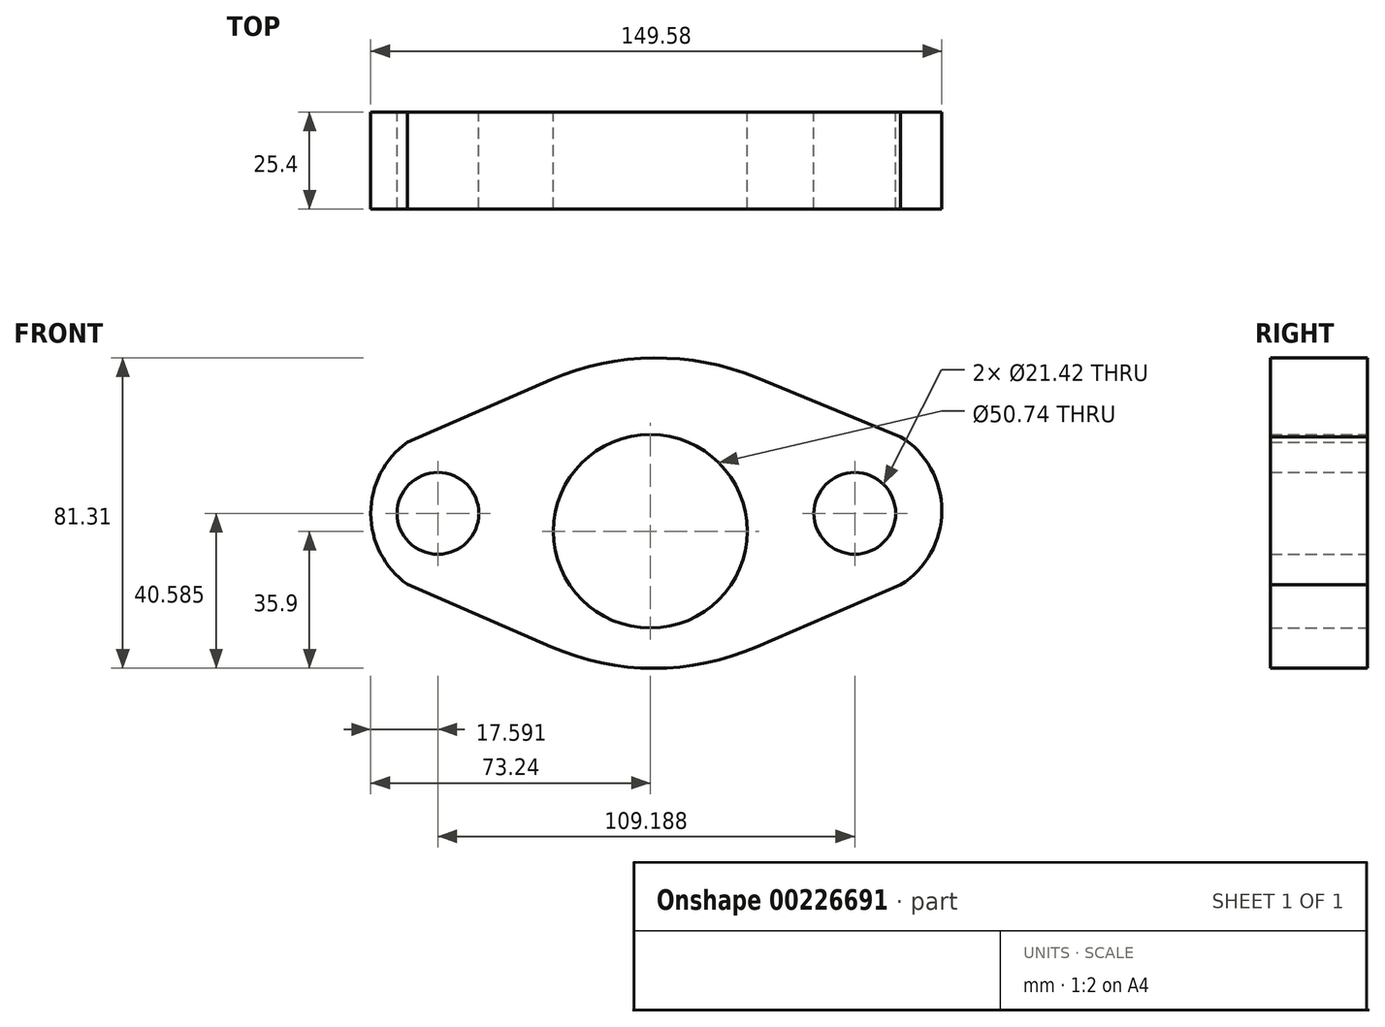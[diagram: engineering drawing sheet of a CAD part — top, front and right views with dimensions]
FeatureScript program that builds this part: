
annotation { "Feature Type Name" : "Feature", "Feature Type Description" : "" }
export const myFeature = defineFeature(function(context is Context, id is Id, definition is map)
    precondition{}
    {
        {
            var Q0;
            Q0=qCreatedBy(makeId("Front.planeOp"),FACE);
            var sketch = newSketch(context, id + "F0", { "sketchPlane" : qUnion([Q0])});
            skCircle(sketch, "E0", {"center": v(0, 0) * mm, "radius": 25.37 * mm});
            skArc(sketch, "E1", {"start": v(27.87, 40.23) * mm, "mid": v(0.85, 45.4) * mm, "end": v(-26.06, 39.65) * mm});
            skLineSegment(sketch, "E2", {"start": v(-26.06, 39.65) * mm, "end": v(-63.66, 23.27) * mm});
            skArc(sketch, "E3", {"start": v(-63.66, 23.27) * mm, "mid": v(-73.24, 4.68) * mm, "end": v(-63.66, -13.9) * mm});
            skLineSegment(sketch, "E4", {"start": v(27.87, 40.23) * mm, "end": v(65.52, 24.79) * mm});
            skLineSegment(sketch, "E5", {"start": v(-63.66, -13.9) * mm, "end": v(-26.06, -30.28) * mm});
            skArc(sketch, "E6", {"start": v(-26.06, -30.28) * mm, "mid": v(0.9, -35.9) * mm, "end": v(27.87, -30.28) * mm});
            skArc(sketch, "E7", {"start": v(65.52, -14.02) * mm, "mid": v(76.34, 5.38) * mm, "end": v(65.52, 24.79) * mm});
            skLineSegment(sketch, "E8", {"start": v(27.87, -30.28) * mm, "end": v(65.52, -14.02) * mm});
            skCircle(sketch, "E9", {"center": v(-55.65, 4.68) * mm, "radius": 10.7 * mm});
            skCircle(sketch, "E10", {"center": v(53.54, 4.68) * mm, "radius": 10.7 * mm});
            skSolve(sketch);
        }
        {
            var Q0;
            Q0 = qSketchRegion(id + "F0", true);
            extrude(context, id + "F1", {"entities" : qUnion([Q0]), "depth" : 25.4 * mm});
        }
    });
